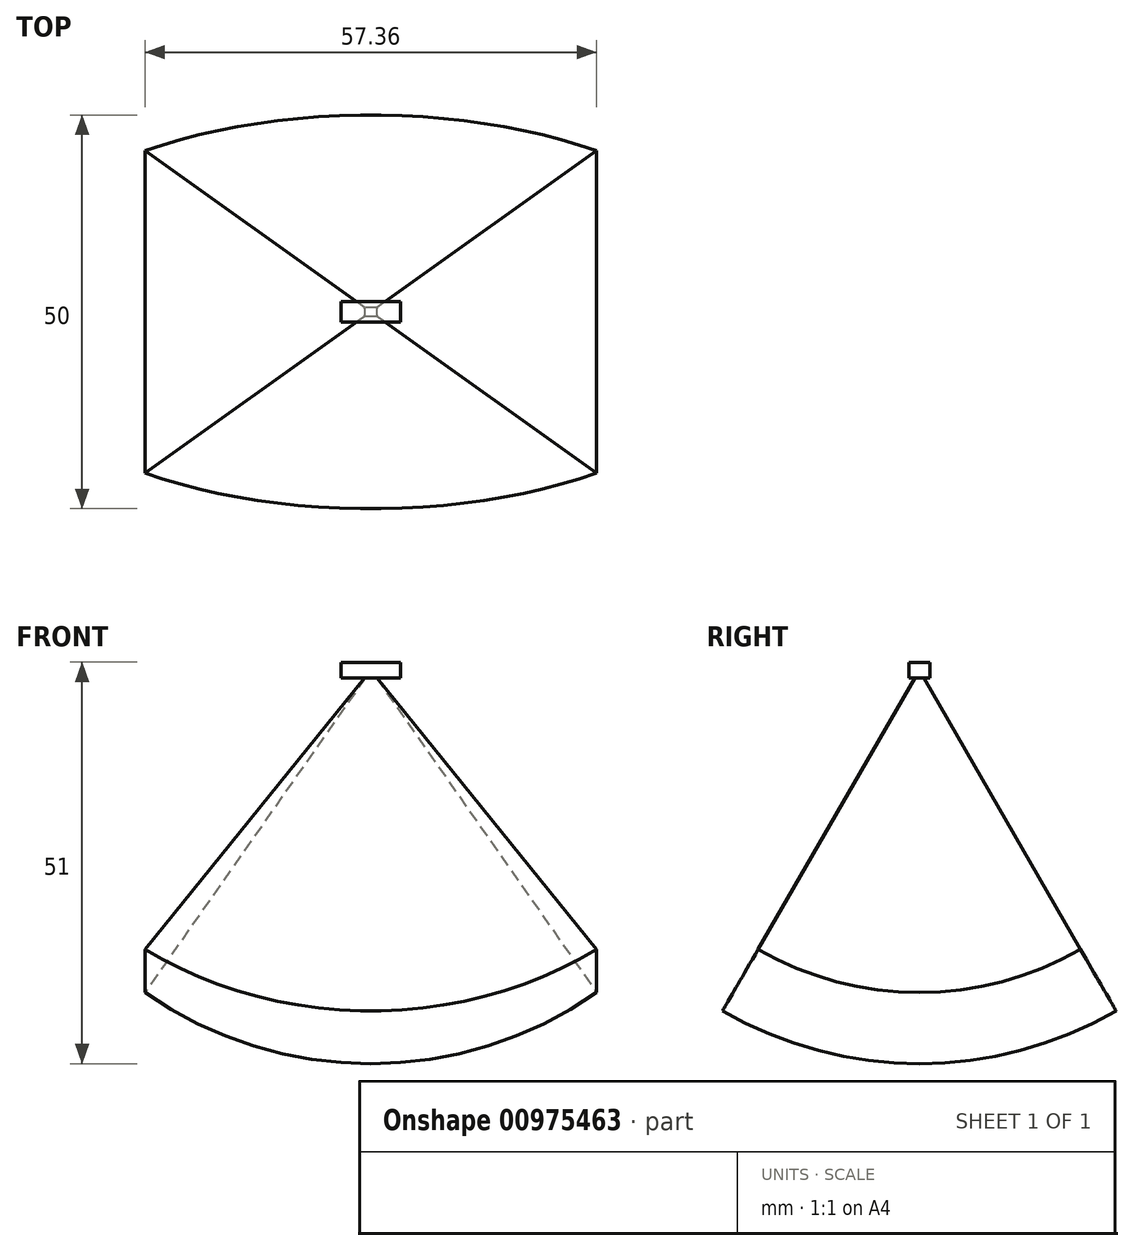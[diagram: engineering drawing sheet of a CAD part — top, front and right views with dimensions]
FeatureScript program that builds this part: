
annotation { "Feature Type Name" : "Feature", "Feature Type Description" : "" }
export const myFeature = defineFeature(function(context is Context, id is Id, definition is map)
    precondition{}
    {
        {
            var Q0;
            Q0=qCreatedBy(makeId("Front.planeOp"),FACE);
            var sketch = newSketch(context, id + "F0", { "sketchPlane" : qUnion([Q0])});
            skLineSegment(sketch, "E0", {"start": v(0, 25.32) * mm, "end": v(-28.68, -15.64) * mm});
            skLineSegment(sketch, "E1", {"start": v(28.68, -15.64) * mm, "end": v(0, 25.32) * mm});
            skArc(sketch, "E2", {"start": v(28.68, -15.64) * mm, "mid": v(0, -24.68) * mm, "end": v(-28.68, -15.64) * mm});
            skPoint(sketch, "E3.end.orphan", {"position": v(0, -15.64) * mm});
            skSolve(sketch);
        }
        {
            var Q0;
            Q0=qCreatedBy(makeId("Top.planeOp"),FACE);
            var Q1;
            Q1=sQuery(id+"F0.wireOp",VERTEX,"E0.start");
            cPlane(context, id + "F1", {"entities" : qUnion([Q0, Q1]), "cplaneType" : CPlaneType.PLANE_POINT, "offset" : 25 * mm, "width" : 150 * mm, "height" : 150 * mm});
        }
        {
            var Q0;
            Q0=qCreatedBy(id+"F1.planeOp",FACE);
            var sketch = newSketch(context, id + "F2", { "sketchPlane" : qUnion([Q0])});
            skLineSegment(sketch, "E4", {"start": v(0, 30.28) * mm, "end": v(0, -37.56) * mm});
            skLineSegment(sketch, "E5", {"start": v(-41.29, 0) * mm, "end": v(47.32, 0) * mm, "construction": true});
            skLineSegment(sketch, "E6.bottom", {"start": v(3.8, 1.31) * mm, "end": v(-3.8, 1.31) * mm});
            skLineSegment(sketch, "E6.top", {"start": v(3.8, -1.31) * mm, "end": v(-3.8, -1.31) * mm});
            skLineSegment(sketch, "E6.left", {"start": v(3.8, 1.31) * mm, "end": v(3.8, -1.31) * mm});
            skLineSegment(sketch, "E6.right", {"start": v(-3.8, 1.31) * mm, "end": v(-3.8, -1.31) * mm});
            skPoint(sketch, "E6.middle", {"position": v(0, 0) * mm});
            skSolve(sketch);
        }
        {
            var Q0;
            Q0=makeQuery(id+"F0.imprint","IMPRINT",FACE,{"disambiguationData":[TD([[makeQuery(id+"F0.imprint","IMPRINT",EDGE,{"derivedFrom":sQuery(id+"F0.wireOp",EDGE,"E0")}),1.0]])]});
            var Q1;
            Q1=sQuery(id+"F2.wireOp",EDGE,"E5");
            revolve(context, id + "F3", {"surfaceOperationType" : NewSurfaceOperationType.NEW, "entities" : qUnion([Q0]), "axis" : qUnion([Q1]), "revolveType" : RevolveType.SYMMETRIC, "angle" : 60 * degree});
        }
        {
            var Q0;
            {var subQ5=sQuery(id+"F2.wireOp",EDGE,"E6.left");Q0=makeQuery(id+"F2.imprint","IMPRINT",FACE,{"disambiguationData":[TD([[makeQuery(id+"F2.imprint","IMPRINT",EDGE,{"derivedFrom":subQ5}),-1.0]])]});}
            var Q1;
            {var subQ5=sQuery(id+"F2.wireOp",EDGE,"E6.right");Q1=makeQuery(id+"F2.imprint","IMPRINT",FACE,{"disambiguationData":[TD([[makeQuery(id+"F2.imprint","IMPRINT",EDGE,{"derivedFrom":subQ5}),1.0]])]});}
            extrude(context, id + "F4", {"entities" : qUnion([Q0, Q1]), "operationType" : NewBodyOperationType.ADD, "depth" : 2 * mm, "offsetDistance" : 25 * mm, "symmetric" : true});
        }
    });
